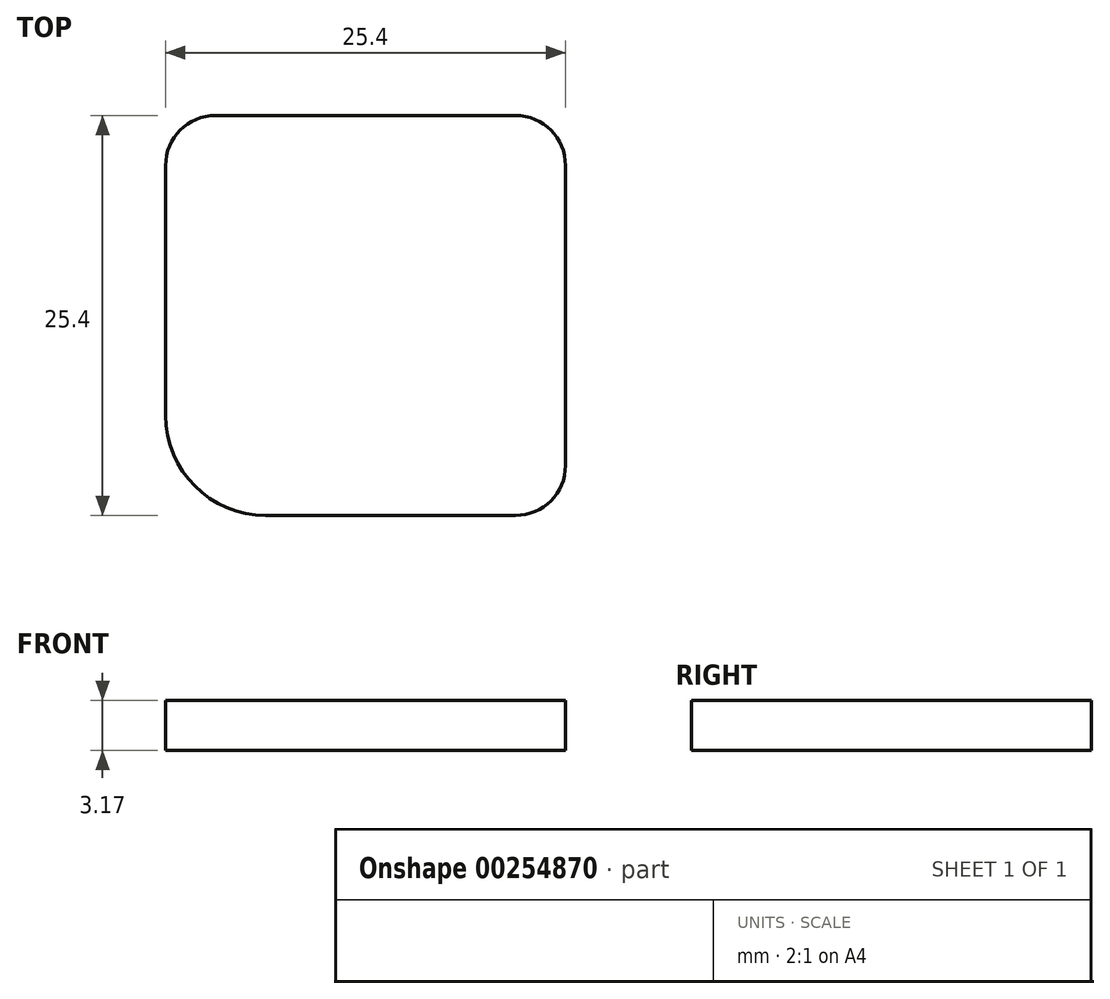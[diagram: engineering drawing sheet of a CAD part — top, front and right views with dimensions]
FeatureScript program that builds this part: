
annotation { "Feature Type Name" : "Feature", "Feature Type Description" : "" }
export const myFeature = defineFeature(function(context is Context, id is Id, definition is map)
    precondition{}
    {
        {
            var Q0;
            Q0=qCreatedBy(makeId("Top.planeOp"),FACE);
            var sketch = newSketch(context, id + "F0", { "sketchPlane" : qUnion([Q0])});
            skLineSegment(sketch, "E0.bottom", {"start": v(9.52, 12.7) * mm, "end": v(-9.53, 12.7) * mm});
            skLineSegment(sketch, "E0.top", {"start": v(9.53, -12.7) * mm, "end": v(-6.35, -12.7) * mm});
            skLineSegment(sketch, "E0.left", {"start": v(12.7, 9.53) * mm, "end": v(12.7, -9.52) * mm});
            skLineSegment(sketch, "E0.right", {"start": v(-12.7, 9.53) * mm, "end": v(-12.7, -6.35) * mm});
            skPoint(sketch, "E0.middle", {"position": v(0, 0) * mm});
            skPoint(sketch, "E1.visualSharp", {"position": v(-12.7, 12.7) * mm});
            skArc(sketch, "E1.filletArc", {"start": v(-9.53, 12.7) * mm, "mid": v(-11.77, 11.77) * mm, "end": v(-12.7, 9.53) * mm});
            skPoint(sketch, "E2.visualSharp", {"position": v(12.7, 12.7) * mm});
            skArc(sketch, "E2.filletArc", {"start": v(12.7, 9.53) * mm, "mid": v(11.77, 11.77) * mm, "end": v(9.52, 12.7) * mm});
            skPoint(sketch, "E3.visualSharp", {"position": v(-12.7, -12.7) * mm});
            skArc(sketch, "E3.filletArc", {"start": v(-12.7, -6.35) * mm, "mid": v(-10.84, -10.84) * mm, "end": v(-6.35, -12.7) * mm});
            skPoint(sketch, "E4.visualSharp", {"position": v(12.7, -12.7) * mm});
            skArc(sketch, "E4.filletArc", {"start": v(9.53, -12.7) * mm, "mid": v(11.77, -11.77) * mm, "end": v(12.7, -9.52) * mm});
            skSolve(sketch);
        }
        {
            var Q0;
            Q0=makeQuery(id+"F0.imprint","IMPRINT",FACE,{"disambiguationData":[TD([[makeQuery(id+"F0.imprint","IMPRINT",EDGE,{"derivedFrom":sQuery(id+"F0.wireOp",EDGE,"E0.bottom")}),1.0]])]});
            extrude(context, id + "F1", {"entities" : qUnion([Q0]), "depth" : 3.17 * mm});
        }
    });
